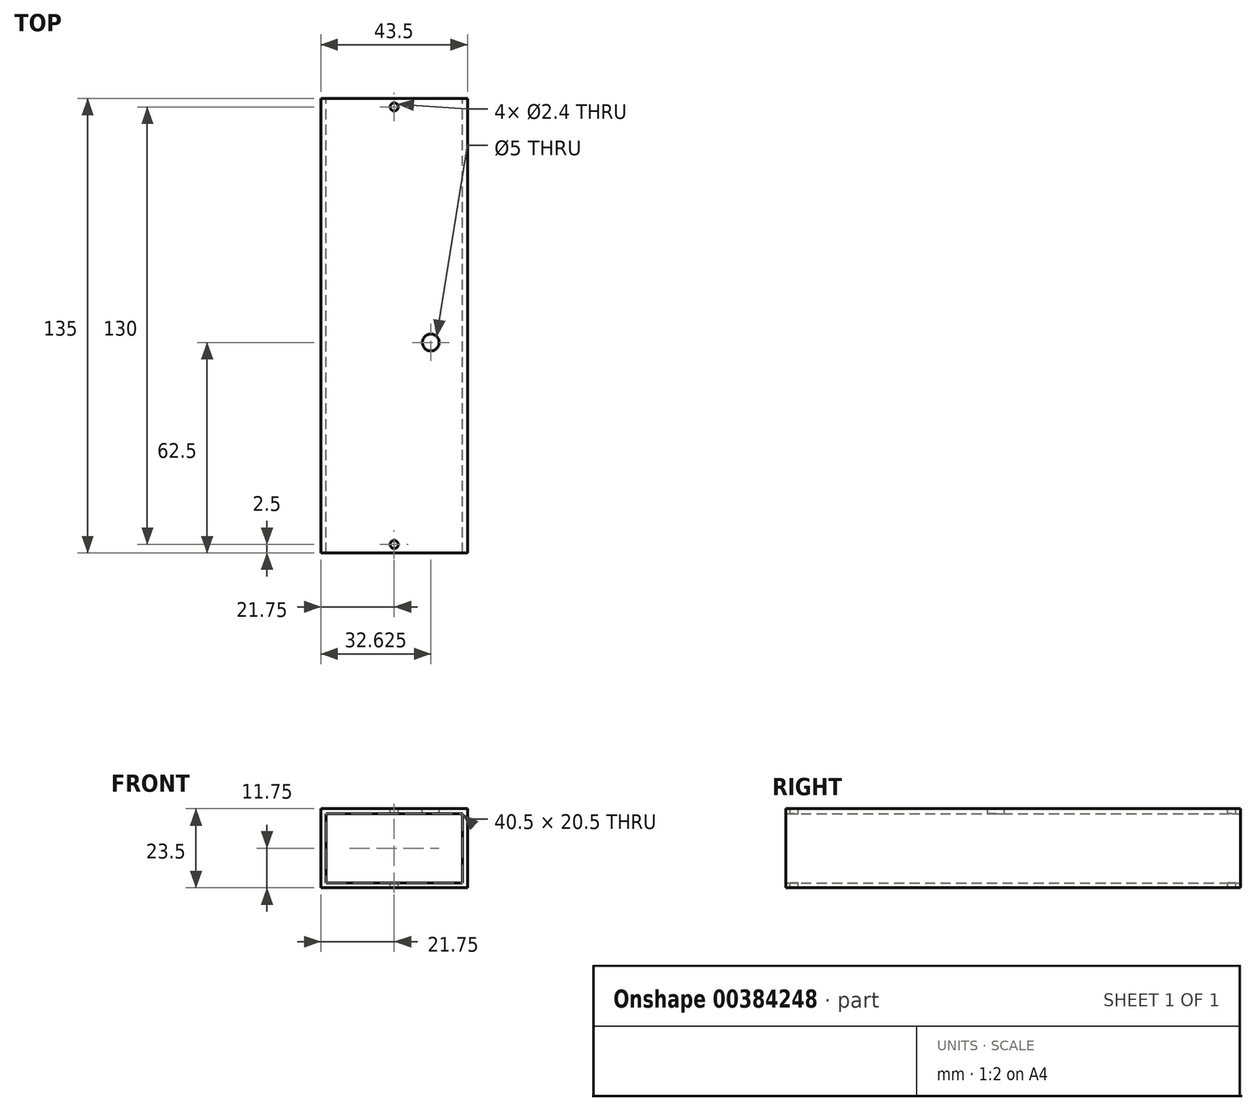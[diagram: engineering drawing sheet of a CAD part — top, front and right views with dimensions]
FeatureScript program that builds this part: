
annotation { "Feature Type Name" : "Feature", "Feature Type Description" : "" }
export const myFeature = defineFeature(function(context is Context, id is Id, definition is map)
    precondition{}
    {
        {
            var Q0;
            Q0=qCreatedBy(makeId("Front.planeOp"),FACE);
            var sketch = newSketch(context, id + "F0", { "sketchPlane" : qUnion([Q0])});
            skLineSegment(sketch, "E0.bottom", {"start": v(21.75, -11.75) * mm, "end": v(-21.75, -11.75) * mm});
            skLineSegment(sketch, "E0.top", {"start": v(21.75, 11.75) * mm, "end": v(-21.75, 11.75) * mm});
            skLineSegment(sketch, "E0.left", {"start": v(21.75, -11.75) * mm, "end": v(21.75, 11.75) * mm});
            skLineSegment(sketch, "E0.right", {"start": v(-21.75, -11.75) * mm, "end": v(-21.75, 11.75) * mm});
            skPoint(sketch, "E0.middle", {"position": v(0, 0) * mm});
            skLineSegment(sketch, "E1.0", {"start": v(20.25, 10.25) * mm, "end": v(-20.25, 10.25) * mm});
            skLineSegment(sketch, "E1.1", {"start": v(20.25, -10.25) * mm, "end": v(20.25, 10.25) * mm});
            skLineSegment(sketch, "E1.2", {"start": v(20.25, -10.25) * mm, "end": v(-20.25, -10.25) * mm});
            skLineSegment(sketch, "E1.3", {"start": v(-20.25, -10.25) * mm, "end": v(-20.25, 10.25) * mm});
            skSolve(sketch);
        }
        {
            var Q0;
            Q0=qSketchRegion(id+"F0",true);
            extrude(context, id + "F1", {"entities" : qUnion([Q0]), "depth" : 135 * mm});
        }
        {
            var Q0;
            Q0=makeQuery(id+"F1.opExtrude","SWEPT_FACE",FACE,{"disambiguationData":[OSD([sQuery(id+"F0.wireOp",EDGE,"E0.top")])]});
            var sketch = newSketch(context, id + "F2", { "sketchPlane" : qUnion([Q0])});
            skCircle(sketch, "E2", {"center": v(10.88, -72.5) * mm, "radius": 2.5 * mm});
            skLineSegment(sketch, "E3", {"start": v(0, -135) * mm, "end": v(0, 0) * mm, "construction": true});
            skLineSegment(sketch, "E4", {"start": v(0, -67.5) * mm, "end": v(21.75, -67.5) * mm, "construction": true});
            skLineSegment(sketch, "E5", {"start": v(10.88, -67.5) * mm, "end": v(10.88, -91.66) * mm, "construction": true});
            skSolve(sketch);
        }
        {
            var Q0;
            Q0=qSketchRegion(id+"F2",true);
            extrude(context, id + "F3", {"entities" : qUnion([Q0]), "operationType" : NewBodyOperationType.REMOVE, "endBound" : BoundingType.UP_TO_NEXT, "oppositeDirection" : true, "depth" : 25 * mm});
        }
        {
            var Q0;
            Q0=makeQuery(id+"F1.opExtrude","SWEPT_FACE",FACE,{"disambiguationData":[OSD([sQuery(id+"F0.wireOp",EDGE,"E0.top")])]});
            var sketch = newSketch(context, id + "F4", { "sketchPlane" : qUnion([Q0])});
            skLineSegment(sketch, "E6", {"start": v(0, -135) * mm, "end": v(0, -130) * mm, "construction": true});
            skPoint(sketch, "E6.endSnap0", {"position": v(0, -135) * mm});
            skCircle(sketch, "E7", {"center": v(0, -132.5) * mm, "radius": 1.2 * mm});
            skLineSegment(sketch, "E8", {"start": v(-21.75, -67.5) * mm, "end": v(21.75, -67.5) * mm, "construction": true});
            skLineSegment(sketch, "E9.MirrorCS", {"start": v(21.75, -67.5) * mm, "end": v(-21.75, -67.5) * mm, "construction": true});
            skCircle(sketch, "E10.MirrorC", {"center": v(0, -2.5) * mm, "radius": 1.2 * mm});
            skSolve(sketch);
        }
        {
            var Q0;
            Q0=qSketchRegion(id+"F4",true);
            extrude(context, id + "F5", {"entities" : qUnion([Q0]), "operationType" : NewBodyOperationType.REMOVE, "oppositeDirection" : true, "depth" : 25 * mm});
        }
    });
